# Revit family: V01023651_Lavamanos Terra
name_source: partatom
category: Plumbing Fixtures
units: mm (PartAtom-declared; Revit-internal decimal feet)

## family parameters
Cut with Voids When Loaded = No
Host = Face
OmniClass Number = 23.31.13.11
OmniClass Title = Single Sinks
Part Type = Normal
Room Calculation Point = No
Round Connector Dimension = Use Diameter
Shared = No

## types (1)
- V01023651_Lavamanos Terra
    Alto = 140 mm  [stored 0.459318 ft]
    Ancho = 420 mm  [stored 1.37795 ft]
    Color = Transparente
    Creado por = BIMBAU
    Default Elevation = 1219 mm
    Description = Adquiere este producto innovador, con diseño transparente para espacios minimalistas y material en vidrio templado.
    Diámetro = 420 mm  [stored 1.37795 ft]
    Fecha de creación = 06/04/2021
    Garantía = 5 años
    Manufacturer = Corona
    Material = Corona_Vidrio templado terra
    Material 2 = Corona_Acero inoxidable
    Model = Aria
    Peso = 5.5 kg
    Pozo = 3 3/4¨ x 5 1/2¨ (39.6 cm x 14 cm)
    Profundidad = 420 mm  [stored 1.37795 ft]
    Referencia = V01023651
    URL = https://corona.co

note: [stored X ft] marks values corroborated as IEEE doubles in the binary element streams (Revit-internal decimal feet)

## geometry (parser evidence)
native form markers: Sweep x6
no freeform markers — native parametric forms only
